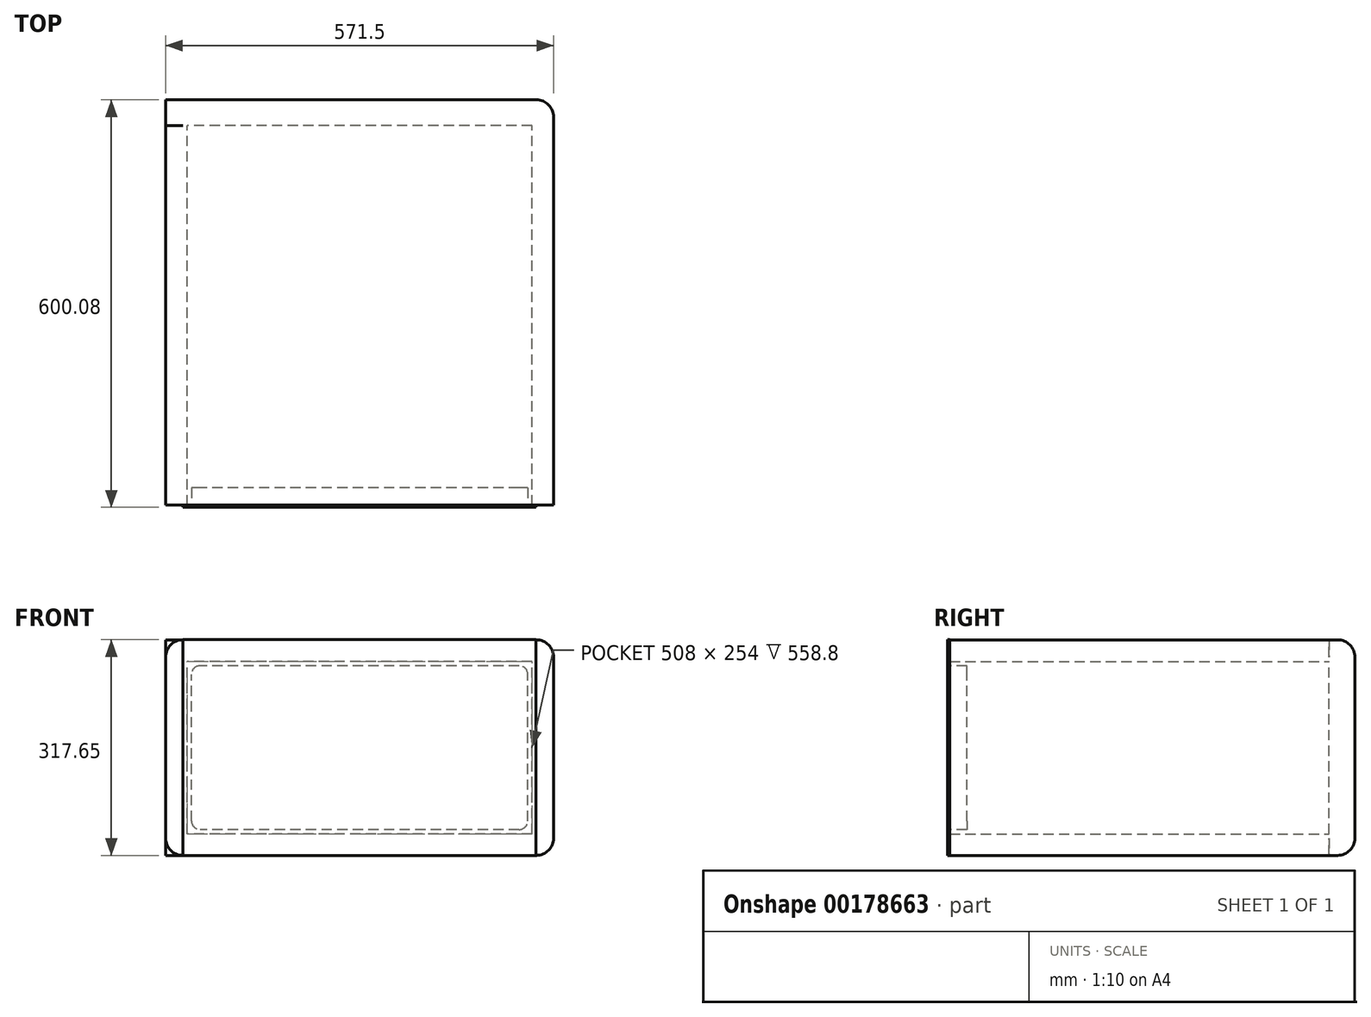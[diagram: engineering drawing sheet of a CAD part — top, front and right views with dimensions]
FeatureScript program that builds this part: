
annotation { "Feature Type Name" : "Feature", "Feature Type Description" : "" }
export const myFeature = defineFeature(function(context is Context, id is Id, definition is map)
    precondition{}
    {
        {
            var Q0;
            Q0=qCreatedBy(makeId("Front.planeOp"),FACE);
            var sketch = newSketch(context, id + "F0", { "sketchPlane" : qUnion([Q0])});
            skLineSegment(sketch, "E0.bottom", {"start": v(254, 31.75) * mm, "end": v(-254, 31.75) * mm});
            skLineSegment(sketch, "E0.top", {"start": v(254, 285.75) * mm, "end": v(-254, 285.75) * mm});
            skLineSegment(sketch, "E0.left", {"start": v(254, 31.75) * mm, "end": v(254, 285.75) * mm});
            skLineSegment(sketch, "E0.right", {"start": v(-254, 31.75) * mm, "end": v(-254, 285.75) * mm});
            skPoint(sketch, "E0.middle", {"position": v(0, 158.75) * mm});
            skLineSegment(sketch, "E1.0", {"start": v(260.35, 317.5) * mm, "end": v(-260.35, 317.5) * mm});
            skLineSegment(sketch, "E2.0", {"start": v(-285.75, 25.4) * mm, "end": v(-285.75, 292.1) * mm});
            skLineSegment(sketch, "E3.0", {"start": v(285.75, 25.4) * mm, "end": v(285.75, 292.1) * mm});
            skLineSegment(sketch, "E4.0", {"start": v(260.35, 0) * mm, "end": v(-260.35, 0) * mm});
            skPoint(sketch, "E5", {"position": v(0, 0) * mm});
            skPoint(sketch, "E6.visualSharp", {"position": v(-285.75, 317.5) * mm});
            skArc(sketch, "E6.filletArc", {"start": v(-260.35, 317.5) * mm, "mid": v(-278.31, 310.06) * mm, "end": v(-285.75, 292.1) * mm});
            skPoint(sketch, "E7.visualSharp", {"position": v(285.75, 317.5) * mm});
            skArc(sketch, "E7.filletArc", {"start": v(285.75, 292.1) * mm, "mid": v(278.31, 310.06) * mm, "end": v(260.35, 317.5) * mm});
            skPoint(sketch, "E8.visualSharp", {"position": v(285.75, 0) * mm});
            skArc(sketch, "E8.filletArc", {"start": v(260.35, 0) * mm, "mid": v(278.31, 7.44) * mm, "end": v(285.75, 25.4) * mm});
            skPoint(sketch, "E9.visualSharp", {"position": v(-285.75, 0) * mm});
            skArc(sketch, "E9.filletArc", {"start": v(-285.75, 25.4) * mm, "mid": v(-278.31, 7.44) * mm, "end": v(-260.35, 0) * mm});
            skSolve(sketch);
        }
        {
            var Q0;
            Q0 = qSketchRegion(id + "F0", true);
            extrude(context, id + "F1", {"entities" : qUnion([Q0]), "depth" : 558.8 * mm});
        }
        {
            var Q0;
            Q0=makeQuery(id+"F1.opExtrude","SWEPT_FACE",FACE,{"disambiguationData":[OSD([sQuery(id+"F0.wireOp",EDGE,"E3.0")])]});
            var sketch = newSketch(context, id + "F2", { "sketchPlane" : qUnion([Q0])});
            skLineSegment(sketch, "E10.bottom", {"start": v(0, 0) * mm, "end": v(38.1, 0) * mm});
            skLineSegment(sketch, "E10.top", {"start": v(0, 317.5) * mm, "end": v(38.1, 317.5) * mm});
            skLineSegment(sketch, "E10.left", {"start": v(0, 0) * mm, "end": v(0, 317.5) * mm});
            skLineSegment(sketch, "E10.right", {"start": v(38.1, 0) * mm, "end": v(38.1, 317.5) * mm});
            skSolve(sketch);
        }
        {
            var Q0;
            Q0 = qSketchRegion(id + "F2", true);
            var Q1;
            Q1=makeQuery(id+"F1.opExtrude","SWEPT_FACE",FACE,{"disambiguationData":[OSD([sQuery(id+"F0.wireOp",EDGE,"E2.0")])]});
            extrude(context, id + "F3", {"entities" : qUnion([Q0]), "operationType" : NewBodyOperationType.ADD, "endBound" : BoundingType.UP_TO_SURFACE, "oppositeDirection" : true, "endBoundEntityFace" : qUnion([Q1]), "depth" : 25.4 * mm});
        }
        {
            var Q0;
            Q0=makeQuery(id+"F3.opExtrude","SWEPT_EDGE",EDGE,{"disambiguationData":[OSD([sQuery(id+"F2.wireOp",EDGE,"E10.top"),sQuery(id+"F2.wireOp",EDGE,"E10.right")])]});
            var Q1;
            Q1=makeQuery(id+"F3.opExtrude","CAP_EDGE",EDGE,{"disambiguationData":[OSD([sQuery(id+"F2.wireOp",EDGE,"E10.top")])],"isStart":true});
            var Q2;
            Q2=makeQuery(id+"F3.opExtrude","CAP_EDGE",EDGE,{"disambiguationData":[OSD([sQuery(id+"F2.wireOp",EDGE,"E10.right")])],"isStart":true});
            var Q3;
            Q3=makeQuery(id+"F3.opExtrude","TWEAK_EDGE",EDGE,{"derivedFrom":[makeQuery(id+"F1.opExtrude","SWEPT_FACE",FACE,{"disambiguationData":[OSD([sQuery(id+"F0.wireOp",EDGE,"E2.0")])]}),makeQuery(id+"F2.imprint","IMPRINT",EDGE,{"derivedFrom":sQuery(id+"F2.wireOp",EDGE,"E10.top")})]});
            var Q4;
            Q4=makeQuery(id+"F3.opExtrude","SWEPT_EDGE",EDGE,{"disambiguationData":[OSD([sQuery(id+"F2.wireOp",EDGE,"E10.bottom"),sQuery(id+"F2.wireOp",EDGE,"E10.right")])]});
            var Q5;
            Q5=makeQuery(id+"F3.opExtrude","TWEAK_EDGE",EDGE,{"derivedFrom":[makeQuery(id+"F1.opExtrude","SWEPT_FACE",FACE,{"disambiguationData":[OSD([sQuery(id+"F0.wireOp",EDGE,"E2.0")])]}),makeQuery(id+"F2.imprint","IMPRINT",EDGE,{"derivedFrom":sQuery(id+"F2.wireOp",EDGE,"E10.bottom")})]});
            var Q6;
            Q6=makeQuery(id+"F3.opExtrude","TWEAK_EDGE",EDGE,{"derivedFrom":[makeQuery(id+"F1.opExtrude","SWEPT_FACE",FACE,{"disambiguationData":[OSD([sQuery(id+"F0.wireOp",EDGE,"E2.0")])]}),makeQuery(id+"F2.imprint","IMPRINT",EDGE,{"derivedFrom":sQuery(id+"F2.wireOp",EDGE,"E10.right")})]});
            var Q7;
            Q7=makeQuery(id+"F3.opExtrude","CAP_EDGE",EDGE,{"disambiguationData":[OSD([sQuery(id+"F2.wireOp",EDGE,"E10.bottom")])],"isStart":true});
            fillet(context, id + "F4", {"entities" : qUnion([Q0, Q1, Q2, Q3, Q4, Q5, Q6, Q7]), "radius" : 25.4 * mm, "tangentPropagation" : true, "allowEdgeOverflow" : false});
        }
        {
            var Q0;
            Q0=makeQuery(id+"F1.opExtrude","CAP_FACE",FACE,{"disambiguationData":[OSD([sQuery(id+"F0.wireOp",EDGE,"E0.bottom"),sQuery(id+"F0.wireOp",EDGE,"E0.top"),sQuery(id+"F0.wireOp",EDGE,"E0.left"),sQuery(id+"F0.wireOp",EDGE,"E0.right"),sQuery(id+"F0.wireOp",EDGE,"E1.0"),sQuery(id+"F0.wireOp",EDGE,"E2.0"),sQuery(id+"F0.wireOp",EDGE,"E3.0"),sQuery(id+"F0.wireOp",EDGE,"E4.0"),sQuery(id+"F0.wireOp",EDGE,"E6.filletArc"),sQuery(id+"F0.wireOp",EDGE,"E7.filletArc"),sQuery(id+"F0.wireOp",EDGE,"E8.filletArc"),sQuery(id+"F0.wireOp",EDGE,"E9.filletArc")])],"isStart":false});
            var sketch = newSketch(context, id + "F5", { "sketchPlane" : qUnion([Q0])});
            skLineSegment(sketch, "E11.0", {"start": v(-247.65, 50.8) * mm, "end": v(-247.65, 266.7) * mm});
            skLineSegment(sketch, "E11.1", {"start": v(234.95, 38.1) * mm, "end": v(-234.95, 38.1) * mm});
            skLineSegment(sketch, "E11.2", {"start": v(247.65, 50.8) * mm, "end": v(247.65, 266.7) * mm});
            skLineSegment(sketch, "E11.3", {"start": v(234.95, 279.4) * mm, "end": v(-234.95, 279.4) * mm});
            skPoint(sketch, "E12.visualSharp", {"position": v(-247.65, 279.4) * mm});
            skArc(sketch, "E12.filletArc", {"start": v(-234.95, 279.4) * mm, "mid": v(-243.93, 275.68) * mm, "end": v(-247.65, 266.7) * mm});
            skPoint(sketch, "E13.visualSharp", {"position": v(247.65, 279.4) * mm});
            skArc(sketch, "E13.filletArc", {"start": v(247.65, 266.7) * mm, "mid": v(243.93, 275.68) * mm, "end": v(234.95, 279.4) * mm});
            skPoint(sketch, "E14.visualSharp", {"position": v(247.65, 38.1) * mm});
            skArc(sketch, "E14.filletArc", {"start": v(234.95, 38.1) * mm, "mid": v(243.93, 41.82) * mm, "end": v(247.65, 50.8) * mm});
            skPoint(sketch, "E15.visualSharp", {"position": v(-247.65, 38.1) * mm});
            skArc(sketch, "E15.filletArc", {"start": v(-247.65, 50.8) * mm, "mid": v(-243.93, 41.82) * mm, "end": v(-234.95, 38.1) * mm});
            skSolve(sketch);
        }
        {
            var Q0;
            Q0=makeQuery(id+"F5.imprint","IMPRINT",FACE,{"disambiguationData":[TD([[makeQuery(id+"F5.imprint","IMPRINT",EDGE,{"derivedFrom":sQuery(id+"F5.wireOp",EDGE,"E11.0")}),-1.0]])]});
            extrude(context, id + "F6", {"entities" : qUnion([Q0]), "oppositeDirection" : true, "depth" : 25.4 * mm});
        }
        {
            var Q0;
            Q0=makeQuery(id+"F5.imprint","IMPRINT",FACE,{"disambiguationData":[TD([[makeQuery(id+"F5.imprint","IMPRINT",EDGE,{"derivedFrom":sQuery(id+"F5.wireOp",EDGE,"E11.0")}),-1.0]])]});
            var sketch = newSketch(context, id + "F7", { "sketchPlane" : qUnion([Q0])});
            skLineSegment(sketch, "E16", {"start": v(-260.46, 0) * mm, "end": v(-260.46, 317.65) * mm});
            skLineSegment(sketch, "E17", {"start": v(-260.46, 317.65) * mm, "end": v(259.98, 317.65) * mm});
            skLineSegment(sketch, "E18", {"start": v(259.98, 317.65) * mm, "end": v(259.98, 0) * mm});
            skLineSegment(sketch, "E19", {"start": v(259.98, 0) * mm, "end": v(-260.46, 0) * mm});
            skSolve(sketch);
        }
        {
            var Q0;
            Q0 = qSketchRegion(id + "F7", true);
            extrude(context, id + "F8", {"entities" : qUnion([Q0]), "depth" : 3.17 * mm});
        }
    });
